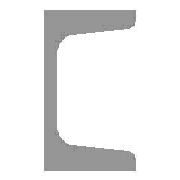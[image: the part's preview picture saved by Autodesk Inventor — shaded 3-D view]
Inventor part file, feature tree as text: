
AUTODESK INVENTOR PART (.ipt)
format: ipt  version: 2025 (Build 290162010, 162A)  size: 140,288 bytes
history: native  units: mm (DEFAULTED — no unit token found)
features: other x4, sketch x1, plane x1
ambient origin geometry x8: Origin, YZ Plane, XZ Plane, XY Plane, X Axis, Y Axis, Z Axis, Center Point
bodies: Solid1 (feature_tree), Body (feature_tree)
feature tree (6):
  parser-record x1  (decoder bookkeeping rows leaked as tree rows — omitted from the tree; the rows remain in map.json)
  other  "Driven Length"
  other  "Start Plane"
  other  "End Plane"
  sketch  "Sketch3"  dims[d0=5.9mm d1=50.0mm d2=50.0mm d3=8.0mm d4=22.05mm d5=2.317543mm d6=2400.0mm d7=0.0mm d23=8.0mm d24=4.5mm d25=1.51mm d26=-0.0mm d27=2400.0mm d28=90.0deg d29=2400.0mm]
  plane  "Work Plane3"
